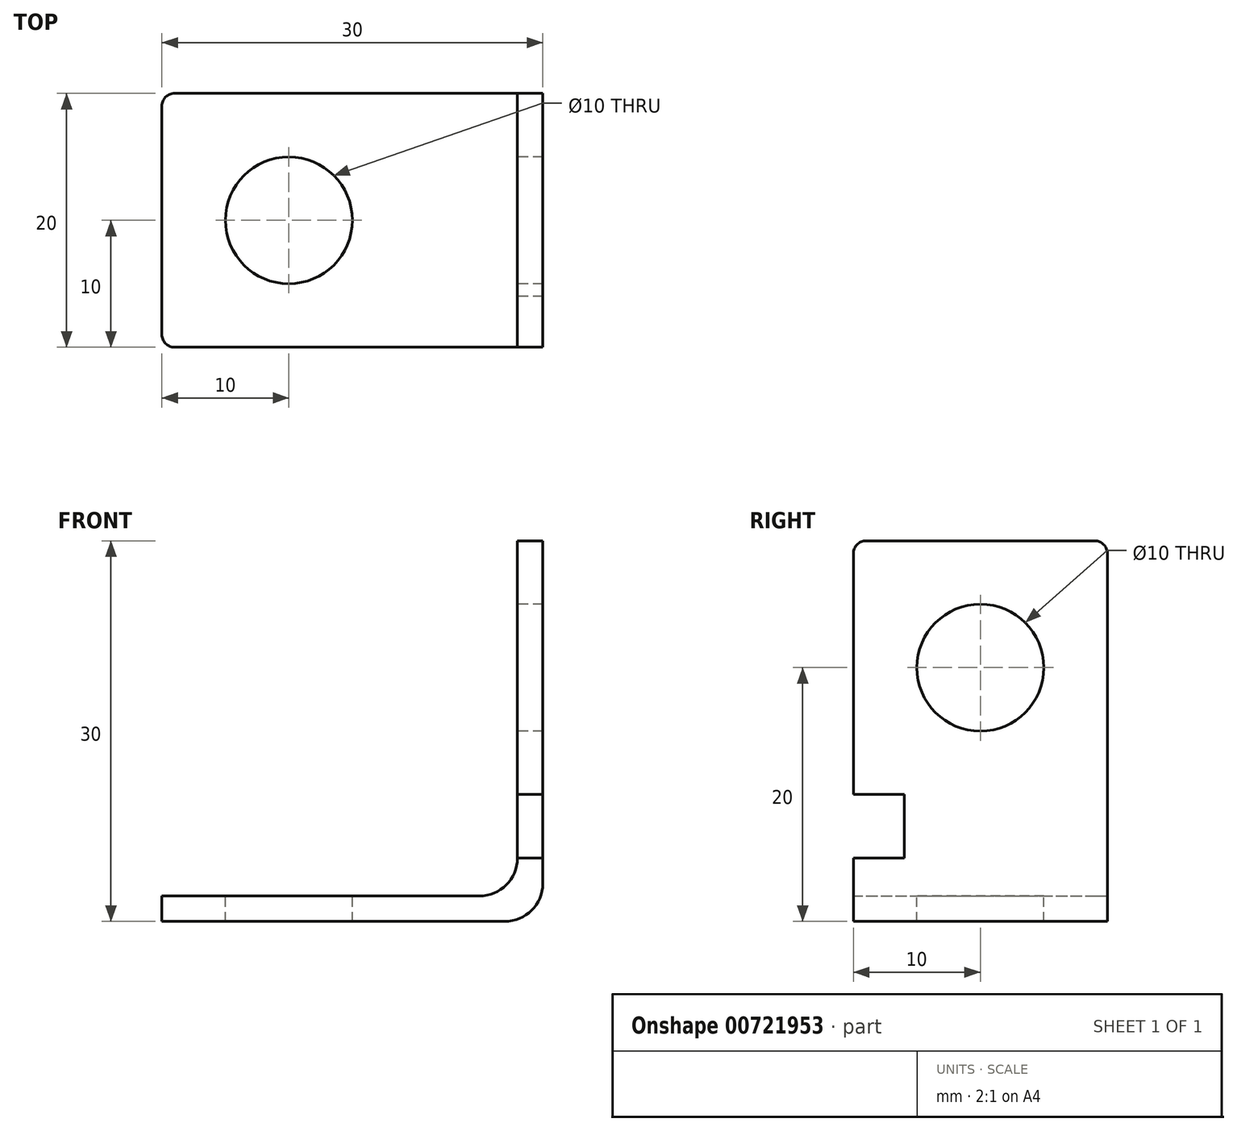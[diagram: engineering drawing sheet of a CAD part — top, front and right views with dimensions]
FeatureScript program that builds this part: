
annotation { "Feature Type Name" : "Feature", "Feature Type Description" : "" }
export const myFeature = defineFeature(function(context is Context, id is Id, definition is map)
    precondition{}
    {
        {
            var Q0;
            Q0=qCreatedBy(makeId("Front.planeOp"),FACE);
            var sketch = newSketch(context, id + "F0", { "sketchPlane" : qUnion([Q0])});
            skLineSegment(sketch, "E0", {"start": v(0, 0) * mm, "end": v(27, 0) * mm});
            skLineSegment(sketch, "E1", {"start": v(30, 3) * mm, "end": v(30, 30) * mm});
            skLineSegment(sketch, "E2", {"start": v(30, 30) * mm, "end": v(28, 30) * mm});
            skLineSegment(sketch, "E3", {"start": v(28, 30) * mm, "end": v(28, 5) * mm});
            skLineSegment(sketch, "E4", {"start": v(25, 2) * mm, "end": v(0, 2) * mm});
            skLineSegment(sketch, "E5", {"start": v(0, 2) * mm, "end": v(0, 0) * mm});
            skPoint(sketch, "E6.visualSharp", {"position": v(30, 0) * mm});
            skArc(sketch, "E6.filletArc", {"start": v(27, 0) * mm, "mid": v(29.12, 0.88) * mm, "end": v(30, 3) * mm});
            skPoint(sketch, "E7.visualSharp", {"position": v(28, 2) * mm});
            skArc(sketch, "E7.filletArc", {"start": v(25, 2) * mm, "mid": v(27.12, 2.88) * mm, "end": v(28, 5) * mm});
            skSolve(sketch);
        }
        {
            var Q0;
            Q0=qSketchRegion(id+"F0",true);
            extrude(context, id + "F1", {"entities" : qUnion([Q0]), "depth" : 20 * mm, "offsetDistance" : 25 * mm});
        }
        {
            var Q0;
            Q0=makeQuery(id+"F1.opExtrude","SWEPT_FACE",FACE,{"disambiguationData":[OSD([sQuery(id+"F0.wireOp",EDGE,"E4")])]});
            var sketch = newSketch(context, id + "F2", { "sketchPlane" : qUnion([Q0])});
            skCircle(sketch, "E8", {"center": v(10, -10) * mm, "radius": 5 * mm});
            skSolve(sketch);
        }
        {
            var Q0;
            Q0=qSketchRegion(id+"F2",true);
            extrude(context, id + "F3", {"entities" : qUnion([Q0]), "operationType" : NewBodyOperationType.REMOVE, "endBound" : BoundingType.THROUGH_ALL, "oppositeDirection" : true, "depth" : 25 * mm, "offsetDistance" : 25 * mm});
        }
        {
            var Q0;
            Q0=makeQuery(id+"F1.opExtrude","SWEPT_FACE",FACE,{"disambiguationData":[OSD([sQuery(id+"F0.wireOp",EDGE,"E3")])]});
            var sketch = newSketch(context, id + "F4", { "sketchPlane" : qUnion([Q0])});
            skCircle(sketch, "E9", {"center": v(10, 20) * mm, "radius": 5 * mm});
            skLineSegment(sketch, "E10.bottom", {"start": v(16, 5) * mm, "end": v(20, 5) * mm});
            skLineSegment(sketch, "E10.top", {"start": v(16, 10) * mm, "end": v(20, 10) * mm});
            skLineSegment(sketch, "E10.left", {"start": v(16, 5) * mm, "end": v(16, 10) * mm});
            skLineSegment(sketch, "E10.right", {"start": v(20, 5) * mm, "end": v(20, 10) * mm});
            skSolve(sketch);
        }
        {
            var Q0;
            Q0=qSketchRegion(id+"F4",true);
            extrude(context, id + "F5", {"entities" : qUnion([Q0]), "operationType" : NewBodyOperationType.REMOVE, "endBound" : BoundingType.THROUGH_ALL, "oppositeDirection" : true, "depth" : 25 * mm, "offsetDistance" : 25 * mm});
        }
        {
            var Q0;
            Q0=makeQuery(id+"F1.opExtrude","CAP_EDGE",EDGE,{"disambiguationData":[OSD([sQuery(id+"F0.wireOp",EDGE,"E5")])],"isStart":false});
            var Q1;
            Q1=makeQuery(id+"F1.opExtrude","CAP_EDGE",EDGE,{"disambiguationData":[OSD([sQuery(id+"F0.wireOp",EDGE,"E2")])],"isStart":false});
            var Q2;
            Q2=makeQuery(id+"F1.opExtrude","CAP_EDGE",EDGE,{"disambiguationData":[OSD([sQuery(id+"F0.wireOp",EDGE,"E2")])],"isStart":true});
            var Q3;
            Q3=makeQuery(id+"F1.opExtrude","CAP_EDGE",EDGE,{"disambiguationData":[OSD([sQuery(id+"F0.wireOp",EDGE,"E5")])],"isStart":true});
            fillet(context, id + "F6", {"entities" : qUnion([Q0, Q1, Q2, Q3]), "radius" : 1 * mm, "tangentPropagation" : true, "allowEdgeOverflow" : false});
        }
    });
